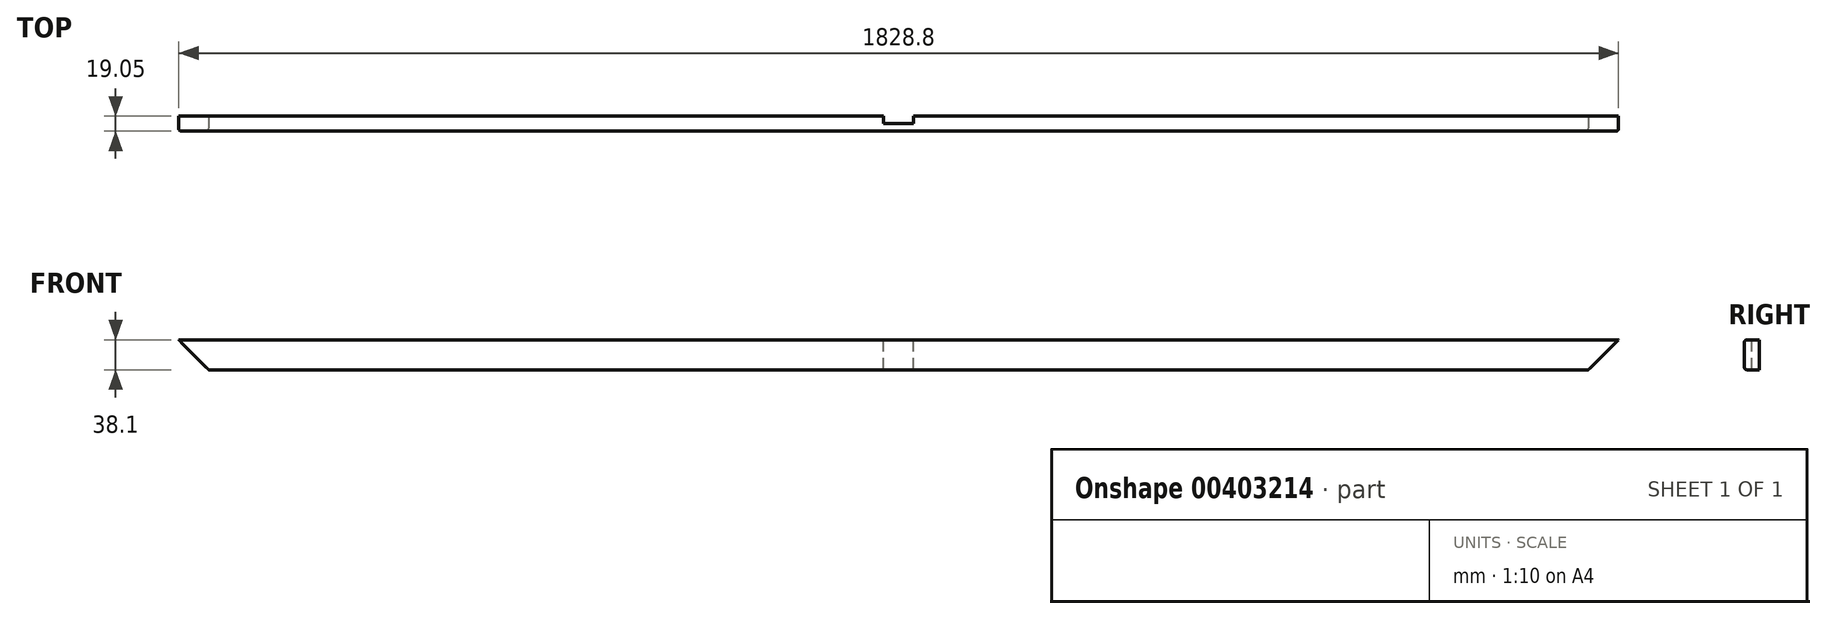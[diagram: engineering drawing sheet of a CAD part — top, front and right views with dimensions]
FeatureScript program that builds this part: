
annotation { "Feature Type Name" : "Feature", "Feature Type Description" : "" }
export const myFeature = defineFeature(function(context is Context, id is Id, definition is map)
    precondition{}
    {
        {
            var Q0;
            Q0=qCreatedBy(makeId("Front.planeOp"),FACE);
            var sketch = newSketch(context, id + "F0", { "sketchPlane" : qUnion([Q0])});
            skLineSegment(sketch, "E0.bottom", {"start": v(914.4, -19.05) * mm, "end": v(-914.4, -19.05) * mm});
            skLineSegment(sketch, "E0.top", {"start": v(914.4, 19.05) * mm, "end": v(-914.4, 19.05) * mm});
            skLineSegment(sketch, "E0.left", {"start": v(914.4, -19.05) * mm, "end": v(914.4, 19.05) * mm});
            skLineSegment(sketch, "E0.right", {"start": v(-914.4, -19.05) * mm, "end": v(-914.4, 19.05) * mm});
            skPoint(sketch, "E0.middle", {"position": v(0, 0) * mm});
            skSolve(sketch);
        }
        {
            var Q0;
            Q0=qSketchRegion(id+"F0",true);
            extrude(context, id + "F1", {"entities" : qUnion([Q0]), "depth" : 19.05 * mm});
        }
        {
            var Q0;
            Q0=makeQuery(id+"F1.opExtrude","CAP_FACE",FACE,{"disambiguationData":[OSD([sQuery(id+"F0.wireOp",EDGE,"E0.bottom"),sQuery(id+"F0.wireOp",EDGE,"E0.top"),sQuery(id+"F0.wireOp",EDGE,"E0.left"),sQuery(id+"F0.wireOp",EDGE,"E0.right")])],"isStart":true});
            var sketch = newSketch(context, id + "F2", { "sketchPlane" : qUnion([Q0])});
            skLineSegment(sketch, "E1.bottom", {"start": v(19.05, -19.05) * mm, "end": v(-19.05, -19.05) * mm});
            skLineSegment(sketch, "E1.top", {"start": v(19.05, 19.05) * mm, "end": v(-19.05, 19.05) * mm});
            skLineSegment(sketch, "E1.left", {"start": v(19.05, -19.05) * mm, "end": v(19.05, 19.05) * mm});
            skLineSegment(sketch, "E1.right", {"start": v(-19.05, -19.05) * mm, "end": v(-19.05, 19.05) * mm});
            skPoint(sketch, "E1.middle", {"position": v(0, 0) * mm});
            skSolve(sketch);
        }
        {
            var Q0;
            Q0 = qSketchRegion(id + "F2", true);
            extrude(context, id + "F3", {"entities" : qUnion([Q0]), "operationType" : NewBodyOperationType.REMOVE, "oppositeDirection" : true, "depth" : 9.52 * mm});
        }
        {
            var Q0;
            Q0=makeQuery(id+"F1.opExtrude","CAP_FACE",FACE,{"disambiguationData":[OSD([sQuery(id+"F0.wireOp",EDGE,"E0.bottom"),sQuery(id+"F0.wireOp",EDGE,"E0.top"),sQuery(id+"F0.wireOp",EDGE,"E0.left"),sQuery(id+"F0.wireOp",EDGE,"E0.right")])],"isStart":false});
            var sketch = newSketch(context, id + "F4", { "sketchPlane" : qUnion([Q0])});
            skLineSegment(sketch, "E2", {"start": v(-914.4, 19.05) * mm, "end": v(-914.4, -19.05) * mm});
            skLineSegment(sketch, "E3", {"start": v(-914.4, -19.05) * mm, "end": v(-876.3, -19.05) * mm});
            skLineSegment(sketch, "E4", {"start": v(-876.3, -19.05) * mm, "end": v(-914.4, 19.05) * mm});
            skLineSegment(sketch, "E5.MirrorCS", {"start": v(914.4, -19.05) * mm, "end": v(876.3, -19.05) * mm});
            skLineSegment(sketch, "E6.MirrorCS", {"start": v(876.3, -19.05) * mm, "end": v(914.4, 19.05) * mm});
            skLineSegment(sketch, "E7.MirrorCS", {"start": v(914.4, 19.05) * mm, "end": v(914.4, -19.05) * mm});
            skSolve(sketch);
        }
        {
            var Q0;
            Q0 = qSketchRegion(id + "F4", true);
            extrude(context, id + "F5", {"entities" : qUnion([Q0]), "operationType" : NewBodyOperationType.REMOVE, "endBound" : BoundingType.THROUGH_ALL, "oppositeDirection" : true, "depth" : 25.4 * mm});
        }
        {
            var Q0;
            Q0=makeQuery(id+"F1.opExtrude","CAP_EDGE",EDGE,{"disambiguationData":[OSD([sQuery(id+"F0.wireOp",EDGE,"E0.top")])],"isStart":false});
            var Q1;
            Q1=makeQuery(id+"F1.opExtrude","CAP_EDGE",EDGE,{"disambiguationData":[OSD([sQuery(id+"F0.wireOp",EDGE,"E0.bottom")])],"isStart":false});
            fillet(context, id + "F6", {"entities" : qUnion([Q0, Q1]), "radius" : 3.17 * mm, "tangentPropagation" : true, "allowEdgeOverflow" : false});
        }
    });
